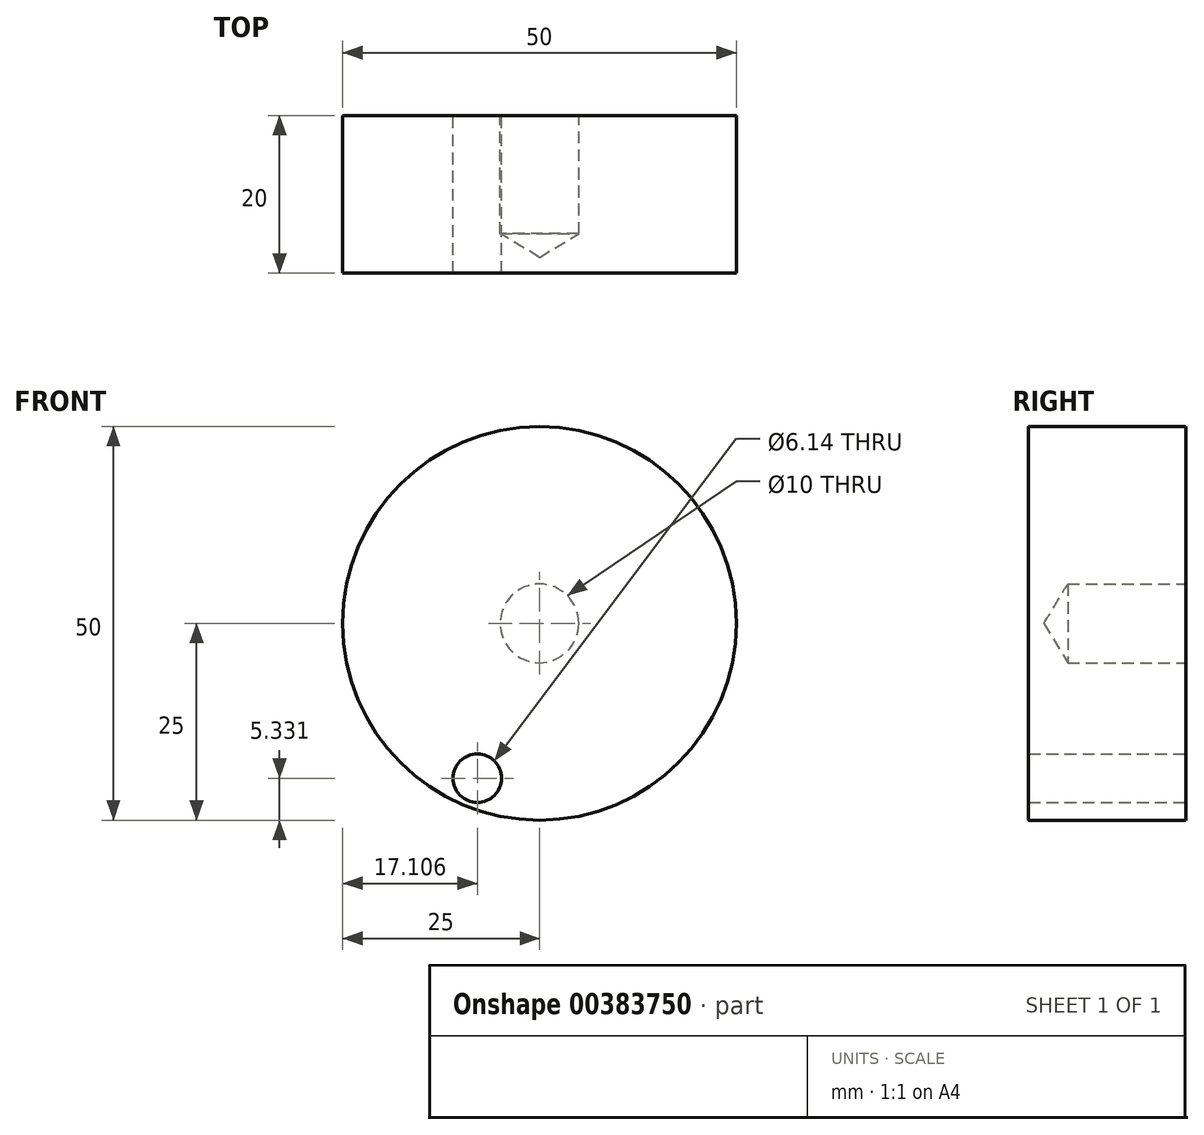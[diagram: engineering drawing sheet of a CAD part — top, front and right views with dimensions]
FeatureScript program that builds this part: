
annotation { "Feature Type Name" : "Feature", "Feature Type Description" : "" }
export const myFeature = defineFeature(function(context is Context, id is Id, definition is map)
    precondition{}
    {
        {
            var Q0;
            Q0=qCreatedBy(makeId("Front.planeOp"),FACE);
            var sketch = newSketch(context, id + "F0", { "sketchPlane" : qUnion([Q0])});
            skCircle(sketch, "E0", {"center": v(0, 0) * mm, "radius": 25 * mm});
            skCircle(sketch, "E1", {"center": v(-7.9, -19.67) * mm, "radius": 3.07 * mm});
            skSolve(sketch);
        }
        {
            var Q0;
            Q0=makeQuery(id+"F0.imprint","IMPRINT",FACE,{"disambiguationData":[TD([[makeQuery(id+"F0.imprint","IMPRINT",EDGE,{"derivedFrom":sQuery(id+"F0.wireOp",EDGE,"E0")}),1.0]])]});
            extrude(context, id + "F1", {"entities" : qUnion([Q0]), "depth" : 20 * mm});
        }
        {
            var Q0;
            Q0=sQuery(id+"F0.wireOp",VERTEX,"E0.center");
            var Q1;
            Q1=makeQuery(id+"F1.opExtrude","SWEPT_BODY",BODY,{"disambiguationData":[OSD([sQuery(id+"F0.wireOp",EDGE,"E0")])]});
            hole(context, id + "F2", {"style" : HoleStyle.SIMPLE, "endStyle" : HoleEndStyle.BLIND, "oppositeDirection" : true, "holeDiameter" : 10 * mm, "holeDepth" : 15 * mm, "isTappedThrough" : true, "tappedDepth" : 12 * mm, "tapClearance" : 3, "locations" : qUnion([Q0]), "scope" : qUnion([Q1])});
        }
    });
